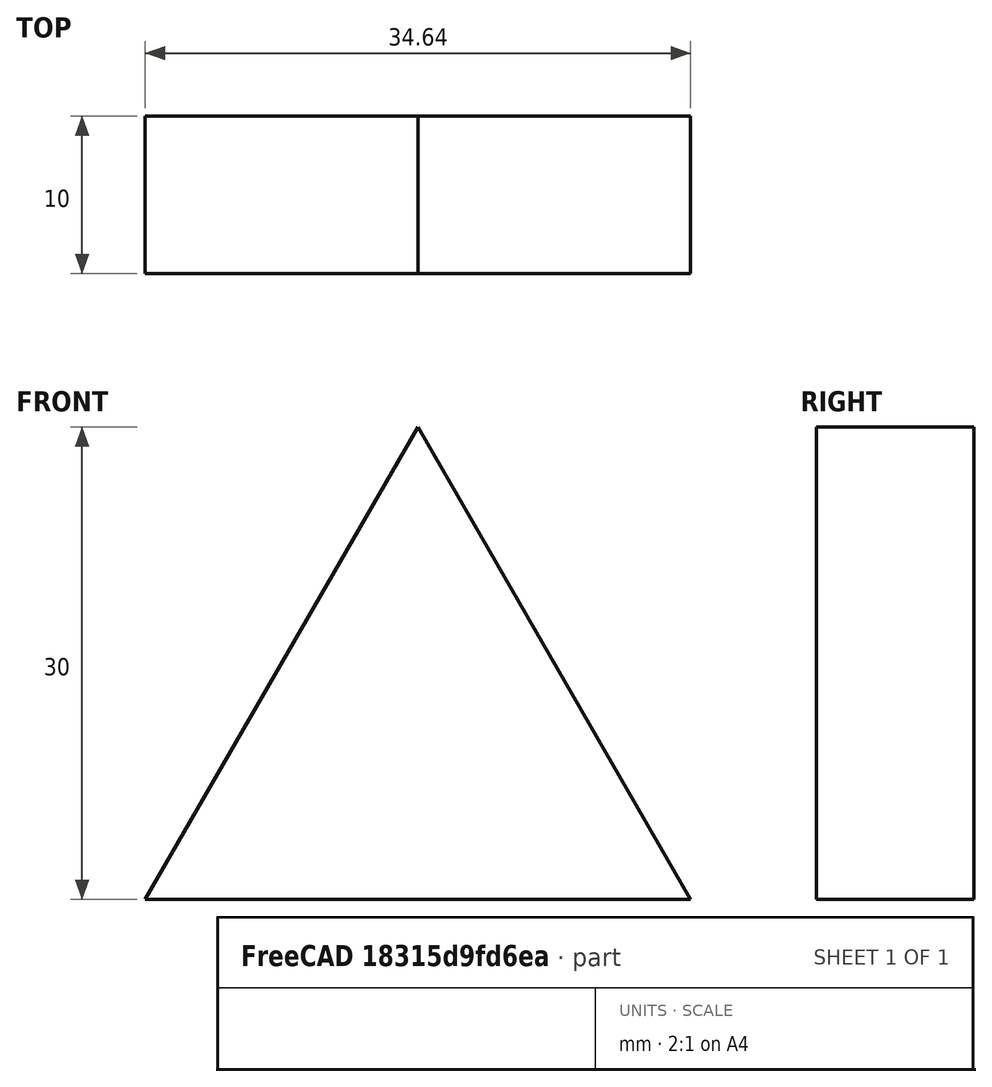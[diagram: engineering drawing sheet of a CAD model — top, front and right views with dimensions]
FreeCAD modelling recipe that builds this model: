
FCSTD DOCUMENT  (FreeCAD 2023.521R14555 (Git shallow))
Label: Triangle
License: All rights reserved
objects: PartDesign::CoordinateSystem×3, Sketcher::SketchObject×1, PartDesign::Pad×1, PartDesign::Body×1, App::Part×1, App::Link×1
note: 9 computed .brp shape members not serialized (recipe doc carries the construction recipe); baked Part::Feature solids carry a one-line shape summary decoded from their .brp
EXTERNAL_REF file=Main_board.FCStd obj=Spreadsheet

FEATURE [PartDesign::CoordinateSystem] LCS_0
  AttacherType = Attacher::AttachEngine3D
  AttachmentSupport = -> [X_Axis]
  InvalidShape = false
  MapMode = 2
  Support = -> [X_Axis]
  TreeRank = 3
  ValidateShape = false
FEATURE [PartDesign::CoordinateSystem] LCS_0001
  AttacherType = Attacher::AttachEngine3D
  AttachmentSupport = -> [X_Axis001]
  InvalidShape = false
  MapMode = 2
  Support = -> [X_Axis001]
  TreeRank = 21
  ValidateShape = false
FEATURE [Sketcher::SketchObject] Sketch
  ArcFitTolerance = 1e-06
  AttachmentSupport = -> [XZ_Plane001]
  ExternalBSplineMaxDegree = 5
  ExternalBSplineTolerance = 0.0001
  FullyConstrained = true
  InternalTolerance = 1e-06
  InvalidShape = false
  MakeInternals = false
  MapMode = 5
  Placement = pos=(0,0,0) rot=(1,0,0;1.5708rad)
  Support = -> [XZ_Plane001]
  TreeRank = 23
  ValidateShape = false
  expr: Constraints[10] = <<dims>>.PS
  sketch-geometry (4):
    g0: LineSegment StartX=17.3205 StartY=-10 StartZ=0 EndX=-7.1e-15 EndY=20 EndZ=0
    g1: LineSegment StartX=-7.8e-15 StartY=20 StartZ=0 EndX=-17.3205 EndY=-10 EndZ=0
    g2: LineSegment StartX=-17.3205 StartY=-10 StartZ=0 EndX=17.3205 EndY=-10 EndZ=0
    g3: Circle [constr] CenterX=0 CenterY=0 CenterZ=0 NormalX=0 NormalY=0 NormalZ=1 AngleXU=0 Radius=20
  constraints (11):
    c: Coincident(g0,g1)
    c: Coincident(g1,g2)
    c: Coincident(g2,g0)
    c: Equal(g0,g1)
    c: Equal(g0,g2)
    c: PointOnObject(g0,g3)
    c: PointOnObject(g1,g3)
    c: PointOnObject(g2,g3)
    c: Coincident(g3,g-1)
    c: Horizontal(g2)
    c: Diameter(g3) = 40
FEATURE [PartDesign::Pad] Pad
  AddSubType = 0
  AlongSketchNormal = false
  AutoTaperInnerAngle = true
  CheckUpToFaceLimits = true
  ClaimChildren = false
  Direction = (0,-1,-2e-16)
  Fit = 0
  FitJoin = 0
  InnerFit = 0
  InnerFitJoin = 0
  InvalidShape = false
  Length = 10
  Length2 = 10
  Linearize = true
  NewSolid = false
  Profile = -> Sketch
  ReferenceAxis = -> Sketch [N_Axis]
  Suppress = false
  TaperInnerAngle = 0
  TaperInnerAngleRev = 0
  TreeRank = 24
  Type = 0
  ValidateShape = true
  _ProfileBasedVersion = 1
FEATURE [PartDesign::CoordinateSystem] Local_CS
  AttacherType = Attacher::AttachEngine3D
  AttachmentSupport = -> [Pad]
  InvalidShape = false
  MapMode = 13
  Placement = pos=(-2.4e-15,-10,-1.66e-14) rot=(1,0,0;1.5708rad)
  Support = -> [Pad]
  TreeRank = 25
  ValidateShape = false
FEATURE [PartDesign::Body] Body
  AutoGroupSolids = false
  ClaimAllChildren = false
  ExportMode = 0
  Group = -> [LCS_0001,Sketch,Pad,Local_CS]
  InvalidShape = false
  Origin = -> Origin001
  Tip = -> Pad
  TreeRank = 22
  ValidateShape = false
  _ExportChildren = -> [LCS_0001,Pad,Local_CS]
  _GroupVersion = 1
FEATURE [App::Part] Triangle
  ClaimAllChildren = false
  ExportMode = 1
  Group = -> [LCS_0,Body]
  Origin = -> Origin
  TreeRank = 11
  _ExportChildren = -> [LCS_0,Body]
  _GroupVersion = 1
FEATURE [App::Link] Link  label="dims"
  AutoLinkLabel = true
  AutoPlacement = true
  LinkedObject = -> <external Main_board.FCStd>#Spreadsheet
  SyncGroupVisibility = false
  TreeRank = 26
  _LinkVersion = 1

RESOLVED EXTERNAL PARTS (link-assembly join: the EXTERNAL_REF files above that resolve inside this repo's crawl, each included once):
---- part Main_board.FCStd = doc fcstd_18a85a5c1fb4 ----
FCSTD DOCUMENT  (FreeCAD 2023.521R14555 (Git shallow))
Label: Main_board
License: All rights reserved
objects: PartDesign::CoordinateSystem×5, Sketcher::SketchObject×2, PartDesign::Pad×1, Spreadsheet::Sheet×1, PartDesign::Body×1, App::Part×1
note: 13 computed .brp shape members not serialized (recipe doc carries the construction recipe); baked Part::Feature solids carry a one-line shape summary decoded from their .brp

FEATURE [Sketcher::SketchObject] Sketch
  ArcFitTolerance = 1e-06
  AttachmentSupport = -> [XZ_Plane]
  ExternalBSplineMaxDegree = 5
  ExternalBSplineTolerance = 0.0001
  FullyConstrained = true
  InternalTolerance = 1e-06
  InvalidShape = false
  MakeInternals = false
  MapMode = 5
  Placement = pos=(0,0,0) rot=(1,0,0;1.5708rad)
  Support = -> [XZ_Plane]
  TreeRank = 11
  ValidateShape = false
  expr: Constraints[48] = <<dims>>.HS
  sketch-geometry (31):
    g0: LineSegment StartX=-40 StartY=19 StartZ=0 EndX=-21.8135 EndY=50.5 EndZ=0
    g1: LineSegment StartX=-21.8135 StartY=50.5 StartZ=0 EndX=-58.1865 EndY=50.5 EndZ=0
    g2: LineSegment StartX=-58.1865 StartY=50.5 StartZ=0 EndX=-40 EndY=19 EndZ=0
    g3: Circle [constr] CenterX=-40 CenterY=40 CenterZ=0 NormalX=0 NormalY=0 NormalZ=1 AngleXU=0 Radius=21
    g4: LineSegment StartX=40 StartY=-19 StartZ=0 EndX=21.8135 EndY=-50.5 EndZ=0
    g5: LineSegment StartX=21.8135 StartY=-50.5 StartZ=0 EndX=58.1865 EndY=-50.5 EndZ=0
    g6: LineSegment StartX=58.1865 StartY=-50.5 StartZ=0 EndX=40 EndY=-19 EndZ=0
    g7: Circle [constr] CenterX=40 CenterY=-40 CenterZ=0 NormalX=0 NormalY=0 NormalZ=1 AngleXU=0 Radius=21
    g8: LineSegment StartX=27.6565 StartY=23.0106 StartZ=0 EndX=52.3435 EndY=23.0106 EndZ=0
    g9: LineSegment StartX=52.3435 StartY=23.0106 StartZ=0 EndX=59.9722 EndY=46.4894 EndZ=0
    g10: LineSegment StartX=59.9722 StartY=46.4894 StartZ=0 EndX=40 EndY=61 EndZ=0
    g11: LineSegment StartX=40 StartY=61 StartZ=0 EndX=20.0278 EndY=46.4894 EndZ=0
    g12: LineSegment StartX=20.0278 StartY=46.4894 StartZ=0 EndX=27.6565 EndY=23.0106 EndZ=0
    g13: Circle [constr] CenterX=40 CenterY=40 CenterZ=0 NormalX=0 NormalY=0 NormalZ=1 AngleXU=0 Radius=21
    g14: LineSegment StartX=-21.8135 StartY=-29.5 StartZ=0 EndX=-40 EndY=-19 EndZ=0
    g15: LineSegment StartX=-40 StartY=-19 StartZ=0 EndX=-58.1865 EndY=-29.5 EndZ=0
    g16: LineSegment StartX=-58.1865 StartY=-29.5 StartZ=0 EndX=-58.1865 EndY=-50.5 EndZ=0
    g17: LineSegment StartX=-58.1865 StartY=-50.5 StartZ=0 EndX=-40 EndY=-61 EndZ=0
    g18: LineSegment StartX=-40 StartY=-61 StartZ=0 EndX=-21.8135 EndY=-50.5 EndZ=0
    g19: LineSegment StartX=-21.8135 StartY=-50.5 StartZ=0 EndX=-21.8135 EndY=-29.5 EndZ=0
    g20: Circle [constr] CenterX=-40 CenterY=-40 CenterZ=0 NormalX=0 NormalY=0 NormalZ=1 AngleXU=0 Radius=21
    g21: Circle CenterX=0 CenterY=0 CenterZ=0 NormalX=0 NormalY=0 NormalZ=1 AngleXU=0 Radius=21
    g22: LineSegment [constr] StartX=-40 StartY=40 StartZ=0 EndX=40 EndY=40 EndZ=0
    g23: LineSegment [constr] StartX=40 StartY=40 StartZ=0 EndX=40 EndY=-40 EndZ=0
    g24: LineSegment [constr] StartX=40 StartY=-40 StartZ=0 EndX=-40 EndY=-40 EndZ=0
    g25: LineSegment [constr] StartX=-40 StartY=-40 StartZ=0 EndX=-40 EndY=40 EndZ=0
    g26: LineSegment StartX=-70 StartY=-70 StartZ=0 EndX=-70 EndY=70 EndZ=0
    g27: LineSegment StartX=-70 StartY=70 StartZ=0 EndX=70 EndY=70 EndZ=0
    g28: LineSegment StartX=70 StartY=70 StartZ=0 EndX=70 EndY=-70 EndZ=0
    g29: LineSegment StartX=70 StartY=-70 StartZ=0 EndX=-70 EndY=-70 EndZ=0
    g30: GeomPoint [constr] X=0 Y=0 Z=0
  constraints (77):
    c: Coincident(g0,g1)
    c: Coincident(g1,g2)
    c: Coincident(g2,g0)
    c: Equal(g0,g1)
    c: Equal(g0,g2)
    c: PointOnObject(g0,g3)
    c: PointOnObject(g1,g3)
    c: PointOnObject(g2,g3)
    c: Coincident(g4,g5)
    c: Coincident(g5,g6)
    c: Coincident(g6,g4)
    c: Equal(g4,g5)
    c: Equal(g4,g6)
    c: PointOnObject(g4,g7)
    c: PointOnObject(g5,g7)
    c: PointOnObject(g6,g7)
    c: Coincident(g8,g9)
    c: Coincident(g9,g10)
    c: Coincident(g10,g11)
    c: Coincident(g11,g12)
    c: Coincident(g12,g8)
    c: Equal(g8, g9-g12) x4
    c: PointOnObject(g8,g13)
    c: PointOnObject(g9,g13)
    c: PointOnObject(g10,g13)
    c: PointOnObject(g11,g13)
    c: PointOnObject(g12,g13)
    c: Coincident(g14,g15)
    c: Coincident(g15,g16)
    c: Coincident(g16,g17)
    c: Coincident(g17,g18)
    c: Coincident(g18,g19)
    c: Coincident(g19,g14)
    c: Equal(g14, g15-g19) x5
    c: PointOnObject(g14,g20)
    c: PointOnObject(g15,g20)
    c: PointOnObject(g16,g20)
    c: PointOnObject(g17,g20)
    c: PointOnObject(g18,g20)
    c: PointOnObject(g19,g20)
    c: Coincident(g21,g-1)
    c: Diameter(g13) = 42
    c: Horizontal(g8)
    c: Equal(g13,g7)
    c: Equal(g7,g20)
    c: Equal(g20,g3)
    c: Vertical(g19)
    c: Horizontal(g5)
    c: Horizontal(g1)
    c: Coincident(g22,g23)
    c: Coincident(g23,g24)
    c: Coincident(g24,g25)
    c: Coincident(g25,g22)
    c: Horizontal(g22)
    c: Horizontal(g24)
    c: Vertical(g23)
    c: Vertical(g25)
    c: Coincident(g22,g3)
    c: Coincident(g23,g7)
    c: Coincident(g22,g13)
    c: Coincident(g24,g20)
    c: Symmetric(g24,g22,g21)
    c: Equal(g23,g24)
    c: DistanceY(g23,g23) = 80
    c: Coincident(g26,g27)
    c: Coincident(g27,g28)
    c: Coincident(g28,g29)
    c: Coincident(g29,g26)
    c: Horizontal(g27)
    c: Horizontal(g29)
    c: Vertical(g26)
    c: Vertical(g28)
    c: Symmetric(g27,g26,g30)
    c: Coincident(g30,g21)
    c: Equal(g28,g29)
    c: DistanceY(g28,g28) = 140
    c: Equal(g21,g13)
FEATURE [PartDesign::Pad] Pad
  AddSubType = 0
  AlongSketchNormal = false
  AutoTaperInnerAngle = true
  CheckUpToFaceLimits = true
  ClaimChildren = false
  Direction = (0,-1,-2e-16)
  Fit = 0
  FitJoin = 0
  InnerFit = 0
  InnerFitJoin = 0
  InvalidShape = false
  Length = 4
  Length2 = 10
  Linearize = true
  NewSolid = false
  Profile = -> Sketch
  ReferenceAxis = -> Sketch [N_Axis]
  Suppress = false
  TaperInnerAngle = 0
  TaperInnerAngleRev = 0
  TreeRank = 12
  Type = 0
  ValidateShape = true
  _ProfileBasedVersion = 1
FEATURE [PartDesign::CoordinateSystem] Local_CS  label="Triangle0"
  AttacherType = Attacher::AttachEngine3D
  AttachmentSupport = -> [Pad]
  InvalidShape = false
  MapMode = 13
  Placement = pos=(-40,-4,40) rot=(1,0,0;1.5708rad)
  Support = -> [Pad]
  TreeRank = 16
  ValidateShape = false
FEATURE [PartDesign::CoordinateSystem] Local_CS002  label="Triangle1"
  AttacherType = Attacher::AttachEngine3D
  AttachmentOffset = pos=(0,0,0) rot=(0,0,1;3.14159rad)
  AttachmentSupport = -> [Pad]
  InvalidShape = false
  MapMode = 13
  Placement = pos=(40,-4,-40) rot=(0,-0.707107,0.707107;3.14159rad)
  Support = -> [Pad]
  TreeRank = 21
  ValidateShape = false
FEATURE [PartDesign::CoordinateSystem] Local_CS003  label="Circle"
  AttacherType = Attacher::AttachEngine3D
  AttachmentSupport = -> [Pad]
  InvalidShape = false
  MapMode = 11
  Placement = pos=(0,-4,-9e-16) rot=(0.57735,-0.57735,0.57735;2.0944rad)
  Support = -> [Pad]
  TreeRank = 22
  ValidateShape = false
FEATURE [Spreadsheet::Sheet] Spreadsheet  label="dims"
  PythonMode = false
  ShowCells = 0
  TreeRank = 25
  cells = A1=Part SIze; B1(PS)==40mm; A2=Gap; B2==2mm; A3=Hole Size; B3(HS)==B1 + B2
FEATURE [Sketcher::SketchObject] Sketch001
  ArcFitTolerance = 1e-06
  AttachmentSupport = -> [Pad]
  ExternalBSplineMaxDegree = 5
  ExternalBSplineTolerance = 0.0001
  ExternalGeometry = -> [Pad]
  FullyConstrained = true
  InternalTolerance = 1e-06
  InvalidShape = false
  MakeInternals = false
  MapMode = 5
  Placement = pos=(0,-4,-9e-16) rot=(1,0,0;1.5708rad)
  Support = -> [Pad]
  TreeRank = 26
  ValidateShape = false
  sketch-geometry (2):
    g0: Circle CenterX=40 CenterY=40 CenterZ=0 NormalX=0 NormalY=0 NormalZ=1 AngleXU=0 Radius=21
    g1: Circle CenterX=-40 CenterY=-40 CenterZ=0 NormalX=0 NormalY=0 NormalZ=1 AngleXU=0 Radius=21
  constraints (6):
    c: PointOnObject(g-4,g0)
    c: PointOnObject(g-3,g0)
    c: PointOnObject(g-3,g0)
    c: PointOnObject(g-5,g1)
    c: PointOnObject(g-6,g1)
    c: PointOnObject(g-6,g1)
FEATURE [PartDesign::Body] Body
  AutoGroupSolids = false
  ClaimAllChildren = false
  ExportMode = 0
  Group = -> [Sketch,Pad,Sketch001]
  InvalidShape = false
  Origin = -> Origin
  Tip = -> Pad
  TreeRank = 10
  ValidateShape = false
  _ExportChildren = -> [Pad,Sketch001]
  _GroupVersion = 1
FEATURE [PartDesign::CoordinateSystem] Local_CS004  label="Penta"
  AttacherType = Attacher::AttachEngine3D
  AttachmentSupport = -> [Sketch001]
  InvalidShape = false
  MapMode = 11
  Placement = pos=(40,-4,40) rot=(-0.57735,0.57735,-0.57735;4.18879rad)
  Support = -> [Sketch001]
  TreeRank = 23
  ValidateShape = false
FEATURE [PartDesign::CoordinateSystem] Local_CS005  label="Hex"
  AttacherType = Attacher::AttachEngine3D
  AttachmentSupport = -> [Sketch001]
  InvalidShape = false
  MapMode = 11
  Placement = pos=(-40,-4,-40) rot=(-0.57735,0.57735,-0.57735;4.18879rad)
  Support = -> [Sketch001]
  TreeRank = 24
  ValidateShape = false
FEATURE [App::Part] Part
  ClaimAllChildren = false
  ExportMode = 1
  Group = -> [Body,Local_CS,Local_CS002,Local_CS003,Local_CS004,Local_CS005]
  Origin = -> Origin001
  TreeRank = 15
  _ExportChildren = -> [Body,Local_CS,Local_CS002,Local_CS003,Local_CS004,Local_CS005]
  _GroupVersion = 1
